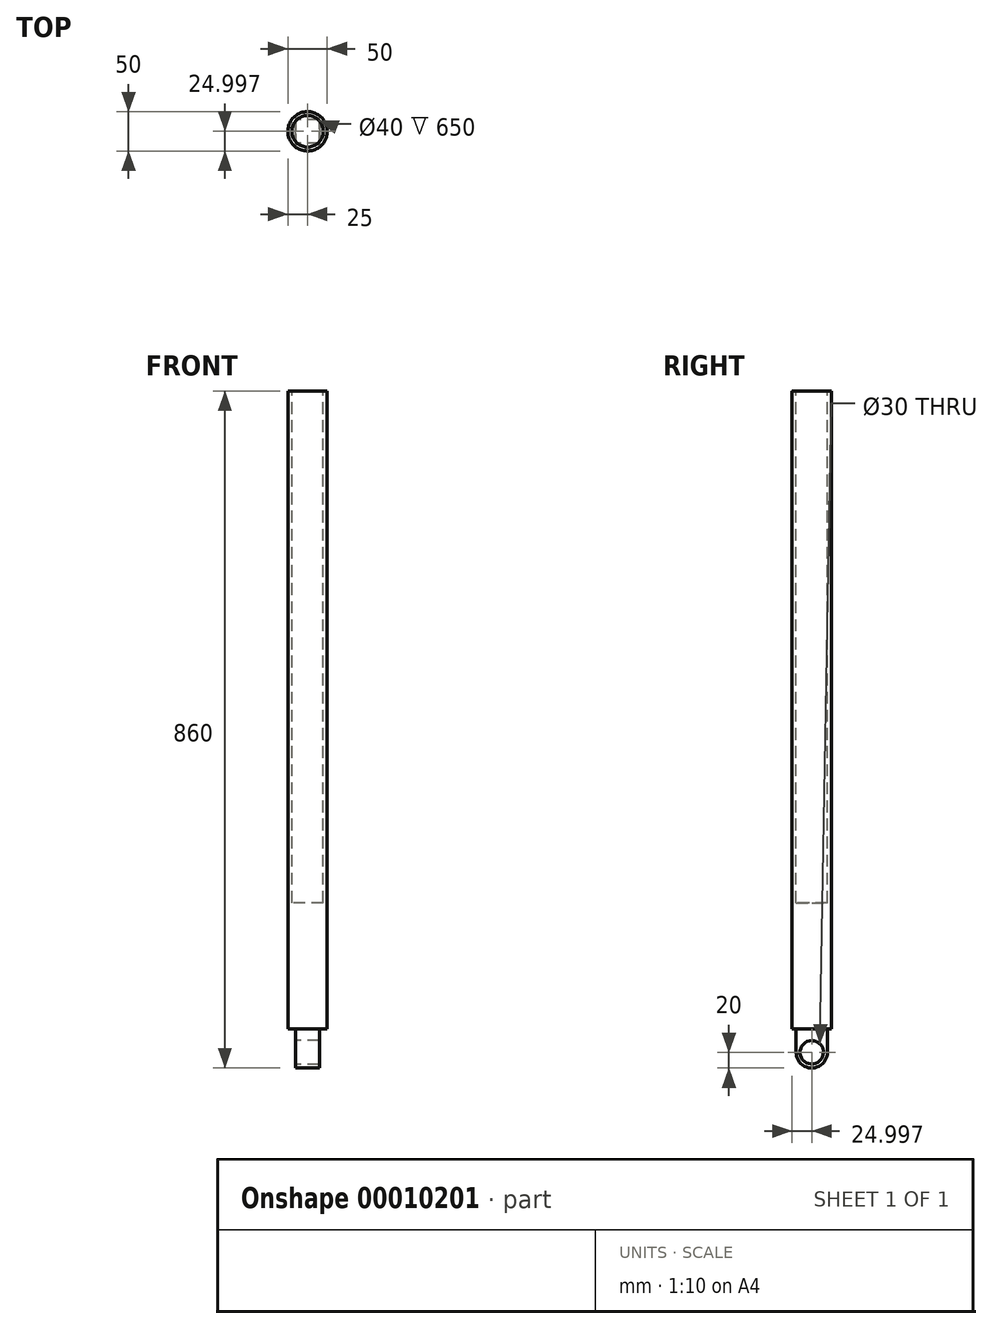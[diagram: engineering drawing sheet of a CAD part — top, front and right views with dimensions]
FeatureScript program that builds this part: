
annotation { "Feature Type Name" : "Feature", "Feature Type Description" : "" }
export const myFeature = defineFeature(function(context is Context, id is Id, definition is map)
    precondition{}
    {
        {
            var Q0;
            Q0=qCreatedBy(makeId("Top.planeOp"),FACE);
            var sketch = newSketch(context, id + "F0", { "sketchPlane" : qUnion([Q0])});
            skCircle(sketch, "E0", {"center": v(0, -15.02) * mm, "radius": 25 * mm});
            skSolve(sketch);
        }
        {
            var Q0;
            Q0 = qSketchRegion(id + "F0", true);
            extrude(context, id + "F1", {"entities" : qUnion([Q0]), "depth" : 810 * mm});
        }
        {
            var Q0;
            Q0=makeQuery(id+"F1.opExtrude","CAP_FACE",FACE,{"disambiguationData":[OSD([sQuery(id+"F0.wireOp",EDGE,"E0")])],"isStart":false});
            var sketch = newSketch(context, id + "F2", { "sketchPlane" : qUnion([Q0])});
            skCircle(sketch, "E1", {"center": v(0, -15.02) * mm, "radius": 20 * mm});
            skSolve(sketch);
        }
        {
            var Q0;
            Q0 = qSketchRegion(id + "F2", true);
            extrude(context, id + "F3", {"entities" : qUnion([Q0]), "operationType" : NewBodyOperationType.REMOVE, "oppositeDirection" : true, "depth" : 650 * mm});
        }
        {
            var Q0;
            Q0=makeQuery(id+"F1.opExtrude","CAP_FACE",FACE,{"disambiguationData":[OSD([sQuery(id+"F0.wireOp",EDGE,"E0")])],"isStart":true});
            var sketch = newSketch(context, id + "F4", { "sketchPlane" : qUnion([Q0])});
            skLineSegment(sketch, "E2", {"start": v(0, 15.02) * mm, "end": v(15, 15.02) * mm, "construction": true});
            skLineSegment(sketch, "E3", {"start": v(-15, -4.98) * mm, "end": v(-15, 35.02) * mm});
            skLineSegment(sketch, "E4", {"start": v(-15, 35.02) * mm, "end": v(15, 35.02) * mm});
            skLineSegment(sketch, "E5", {"start": v(-15, -4.98) * mm, "end": v(15, -4.98) * mm});
            skLineSegment(sketch, "E6", {"start": v(15, 35.02) * mm, "end": v(15, -4.98) * mm});
            skSolve(sketch);
        }
        {
            var Q0;
            Q0 = qSketchRegion(id + "F4", true);
            extrude(context, id + "F5", {"entities" : qUnion([Q0]), "operationType" : NewBodyOperationType.ADD, "depth" : 50 * mm});
        }
        {
            var Q0;
            Q0=makeQuery(id+"F5.opExtrude","SWEPT_FACE",FACE,{"disambiguationData":[OSD([sQuery(id+"F4.wireOp",EDGE,"E3")])]});
            var sketch = newSketch(context, id + "F6", { "sketchPlane" : qUnion([Q0])});
            skLineSegment(sketch, "E7", {"start": v(15.02, -50) * mm, "end": v(15.02, -30) * mm, "construction": true});
            skArc(sketch, "E8", {"start": v(-4.98, -30) * mm, "mid": v(15.02, -50) * mm, "end": v(35.02, -30) * mm});
            skLineSegment(sketch, "E9", {"start": v(15.02, -50) * mm, "end": v(35.02, -50) * mm});
            skLineSegment(sketch, "E10", {"start": v(35.02, -50) * mm, "end": v(35.02, -30) * mm});
            skLineSegment(sketch, "E11", {"start": v(15.02, -50) * mm, "end": v(-4.98, -50) * mm});
            skLineSegment(sketch, "E12", {"start": v(-4.98, -50) * mm, "end": v(-4.98, -30) * mm});
            skLineSegment(sketch, "E13", {"start": v(35.02, -30) * mm, "end": v(-4.98, -30) * mm, "construction": true});
            skCircle(sketch, "E14", {"center": v(15.02, -30) * mm, "radius": 15 * mm});
            skSolve(sketch);
        }
        {
            var Q0;
            Q0 = qSketchRegion(id + "F6", true);
            extrude(context, id + "F7", {"entities" : qUnion([Q0]), "operationType" : NewBodyOperationType.REMOVE, "endBound" : BoundingType.UP_TO_NEXT, "oppositeDirection" : true, "depth" : 25 * mm});
        }
    });
